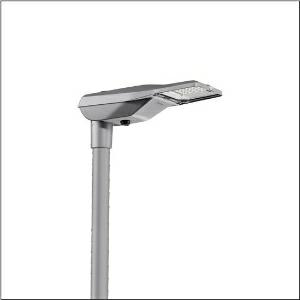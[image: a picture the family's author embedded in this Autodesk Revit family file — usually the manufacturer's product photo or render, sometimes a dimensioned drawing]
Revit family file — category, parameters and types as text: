
# Revit family: streetlight_sl_21_iq_micro___p0_8a_5xe1u31u08db_b9e4
name_source: partatom
category: Lighting Fixtures
units: mm (PartAtom-declared; Revit-internal decimal feet)

## family parameters
Cut with Voids When Loaded = No
Host = Face
Light Source = No
Part Type = Normal
Room Calculation Point = No
Round Connector Dimension = Use Diameter
Shared = No

## types (1)
- --- (1 x LED, 5130 lm, 39.1 W, 3000K)
    Apparent Load = 39 VA
    CIE Flux Codes = 33 69 96 100 100
    Color Rendering = 70
    Color Temperature = 3000K
    Default Elevation = 1800 mm
    Description = Streetlight SL 21 iQ micro, mast luminaire, primary light control with lens, of PMMA, primary optical cover: cover, of toughened safety glass, transparent, light distribution: P0.8a, light emission: direct distribution, primary light characteristic: asymmetric, installation type: post-top, side-entry, LED, High Power LED, rated luminous flux: 5.130lm, luminous efficacy: 131lm/W, light colour: 730, colour temperature: 3000K, control gear: iQ-Street Remote, D4i with power reduction, control: pre-setting: logarithmic dimming characteristic, Street-Remote, Auto-Match, Temp-Guard, Lumen-Switch, Night-Set, Smart-Wire, Light-Fading, Desk-Remote (wireless, voltage-free reading and setting of iQ features in the workshop via application-optimized NFC function/RFID function), optimised constant luminous flux control (CLO 2.0), mains connection: 220..240V, AC, 50/60Hz, start of lifetime: 39W, end of service life: 41W, reduction: 17W, luminaire housing, of diecast aluminium, powder-coated, Siteco® metallic grey (DB 702S), corrosivity category C5 mid according to DIN EN ISO 12944, please order mast flange separately, inclination adjustable: 0°, 5°, 10°, 15°, sealing non-destructively replaceable, multi-level sealing system, length: 528mm, width: 235mm, height: 110mm, mast flange for spigot size: 42mm (side-entry): 5XC10008XM4, 60/48mm (side-entry/post-top): 5XC10108XM2, 76/60mm (side-entry/post-top): 5XC10108XM1, mounting height: 4..8m, Smart Interface below, protection rating (complete): IP66, insulation class (complete): insulation class II (safety insulation), certification: CE, ENEC, ENEC+, VDE, impact resistance: IK09, permissible operating ambient temperature for outdoor applications: -40..+50°C, standard-compliant lighting for roads and squares, packaging unit: 1 piece

Light Distribution: P0.8a
    Height = 110 mm
    Lamp = 1 x LED
    Lamp Light Flux = 5130 lm
    Lamp Power = 39.1 W
    Lamp count = 1
    Length = 528 mm
    Luminous efficacy = 131 lm/W
    Manufacturer = Siteco
    ModVariant = No
    Model = 5XE1U31U08DB
    Number of Poles = 1
    OnlyDefault = Yes
    Power Factor = 1
    Product Name = Streetlight SL 21 iQ micro | P0.8a
    Product group = mast luminaire | pylon top
    ProductGroupID = 6100
    Protection Class = Protection class II
    Protection Degree = IP 66
    RLX_Detail_Level = 1
    RLX_Emergency_Light_Flux = 0 lm
    RLX_Emergency_Type = 0
    RLX_Emergency_Type_DB = No
    RlxData = <blob elided: 99437 chars, md5=63225976>
    Socket = socket
    Standby Power = 0 W
    System Light Flux = 5130 lm
    System Power = 39 W
    Type Comments = factory setting: luminous flux: 100 % | dim-lin: 254 | 765 mA
    Type Image = l_1277290.jpg
    URL = http://relux.com
    VarID = @adj_071338
    Voltage = 0 V
    Weight = 0.00 kg
    Width = 235 mm

## geometry (parser evidence)
native form markers: Blend x4, Sweep x8
no freeform markers — native parametric forms only
